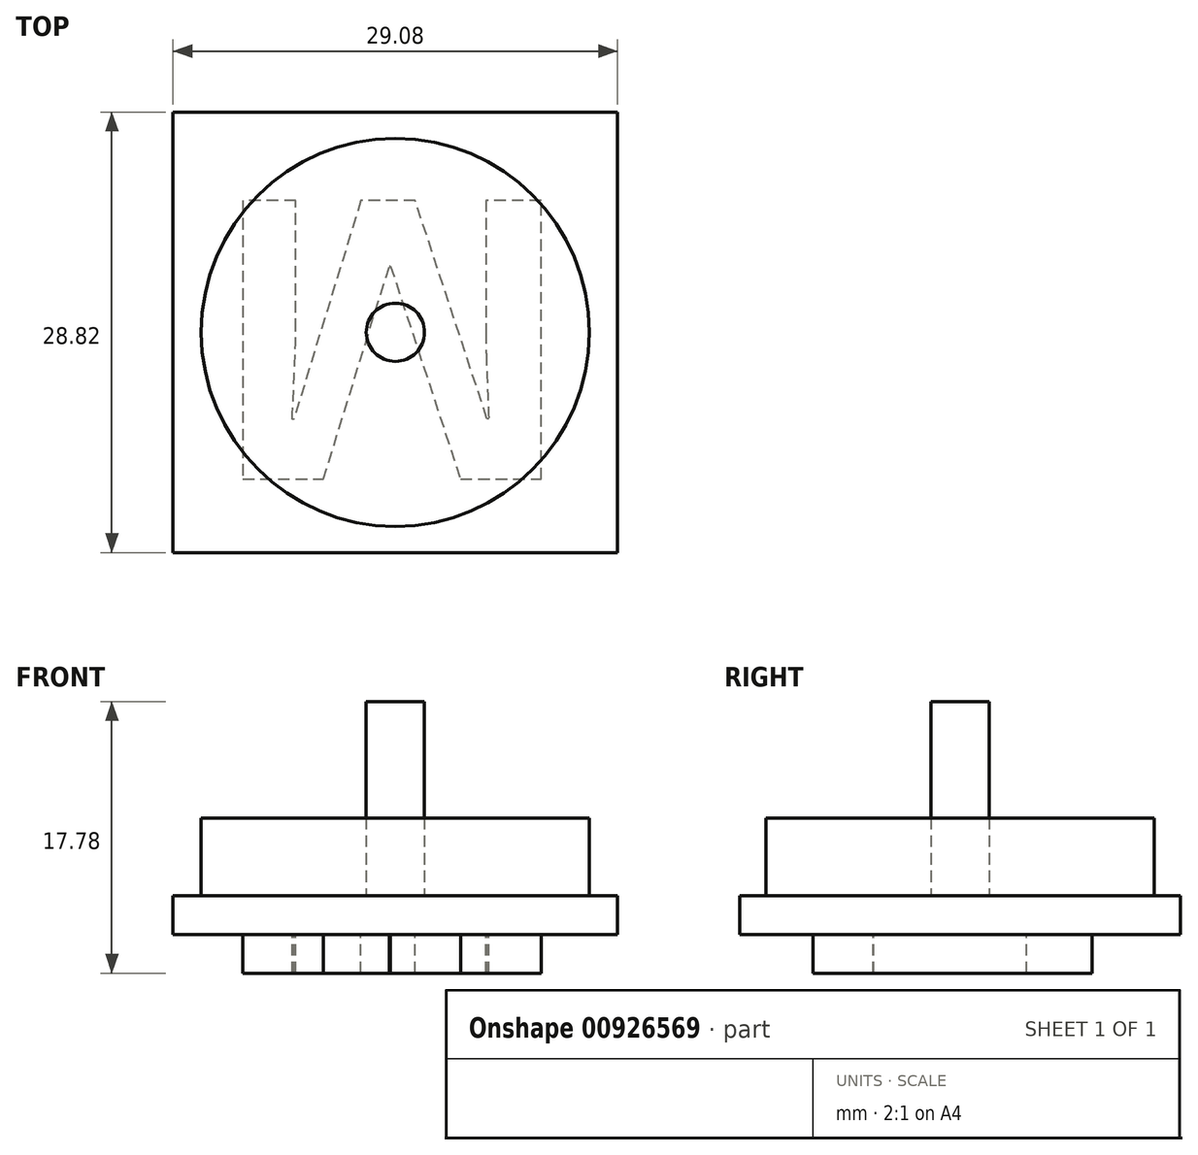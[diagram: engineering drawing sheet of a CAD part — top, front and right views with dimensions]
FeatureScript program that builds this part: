
annotation { "Feature Type Name" : "Feature", "Feature Type Description" : "" }
export const myFeature = defineFeature(function(context is Context, id is Id, definition is map)
    precondition{}
    {
        {
            var Q0;
            Q0=qCreatedBy(makeId("Top.planeOp"),FACE);
            var sketch = newSketch(context, id + "F0", { "sketchPlane" : qUnion([Q0])});
            skCircle(sketch, "E0", {"center": v(0, 0) * mm, "radius": 12.7 * mm});
            skSolve(sketch);
        }
        {
            var Q0;
            Q0=makeQuery(id+"F0.imprint","IMPRINT",FACE,{"disambiguationData":[TD([[makeQuery(id+"F0.imprint","IMPRINT",EDGE,{"derivedFrom":sQuery(id+"F0.wireOp",EDGE,"E0")}),1.0]])]});
            var sketch = newSketch(context, id + "F1", { "sketchPlane" : qUnion([Q0])});
            skCircle(sketch, "E1", {"center": v(0, 0) * mm, "radius": 1.9 * mm});
            skSolve(sketch);
        }
        {
            var Q0;
            Q0=makeQuery(id+"F1.imprint","IMPRINT",FACE,{"disambiguationData":[TD([[makeQuery(id+"F1.imprint","IMPRINT",EDGE,{"derivedFrom":sQuery(id+"F1.wireOp",EDGE,"E1")}),1.0]])]});
            extrude(context, id + "F2", {"entities" : qUnion([Q0]), "depth" : 12.7 * mm, "offsetDistance" : 25.4 * mm});
        }
        {
            var Q0;
            Q0=qCreatedBy(makeId("Top.planeOp"),FACE);
            var sketch = newSketch(context, id + "F3", { "sketchPlane" : qUnion([Q0])});
            skLineSegment(sketch, "E2.bottom", {"start": v(14.54, -14.4) * mm, "end": v(-14.54, -14.4) * mm});
            skLineSegment(sketch, "E2.top", {"start": v(14.54, 14.4) * mm, "end": v(-14.54, 14.4) * mm});
            skLineSegment(sketch, "E2.left", {"start": v(14.54, -14.4) * mm, "end": v(14.54, 14.4) * mm});
            skLineSegment(sketch, "E2.right", {"start": v(-14.54, -14.4) * mm, "end": v(-14.54, 14.4) * mm});
            skPoint(sketch, "E2.middle", {"position": v(0, 0) * mm});
            skSolve(sketch);
        }
        {
            var Q0;
            Q0=makeQuery(id+"F3.imprint","IMPRINT",FACE,{"disambiguationData":[TD([[makeQuery(id+"F3.imprint","IMPRINT",EDGE,{"derivedFrom":sQuery(id+"F3.wireOp",EDGE,"E2.bottom")}),-1.0]])]});
            extrude(context, id + "F4", {"entities" : qUnion([Q0]), "oppositeDirection" : true, "depth" : 2.54 * mm, "offsetDistance" : 25.4 * mm});
        }
        {
            var Q0;
            Q0=makeQuery(id+"F0.imprint","IMPRINT",FACE,{"disambiguationData":[TD([[makeQuery(id+"F0.imprint","IMPRINT",EDGE,{"derivedFrom":sQuery(id+"F0.wireOp",EDGE,"E0")}),1.0]])]});
            extrude(context, id + "F5", {"entities" : qUnion([Q0]), "depth" : 5.08 * mm, "offsetDistance" : 25.4 * mm});
        }
        {
            var Q0;
            Q0=makeQuery(id+"F4.opExtrude","CAP_FACE",FACE,{"disambiguationData":[OSD([sQuery(id+"F3.wireOp",EDGE,"E2.bottom"),sQuery(id+"F3.wireOp",EDGE,"E2.top"),sQuery(id+"F3.wireOp",EDGE,"E2.left"),sQuery(id+"F3.wireOp",EDGE,"E2.right")])],"isStart":false});
            var sketch = newSketch(context, id + "F6", { "sketchPlane" : qUnion([Q0])});
            skText(sketch, "E3", { "text": "M", "fontName": "OpenSans-Bold.ttf"});
            const initialGuessF6  = {"E3": [-0.01227, -0.00863, 1, 0, 0.0184]};
            skSetInitialGuess(sketch, initialGuessF6);
            skSolve(sketch);
        }
        {
            var Q0;
            Q0=makeQuery(id+"F6.imprint","IMPRINT",FACE,{"disambiguationData":[TD([[makeQuery(id+"F6.imprint","IMPRINT",EDGE,{"derivedFrom":sQuery(id+"F6.wireOp",EDGE,"E3.sketch_text.stroke-0")}),-1.0]])]});
            extrude(context, id + "F7", {"entities" : qUnion([Q0]), "operationType" : NewBodyOperationType.ADD, "depth" : 2.54 * mm, "offsetDistance" : 25.4 * mm});
        }
    });
